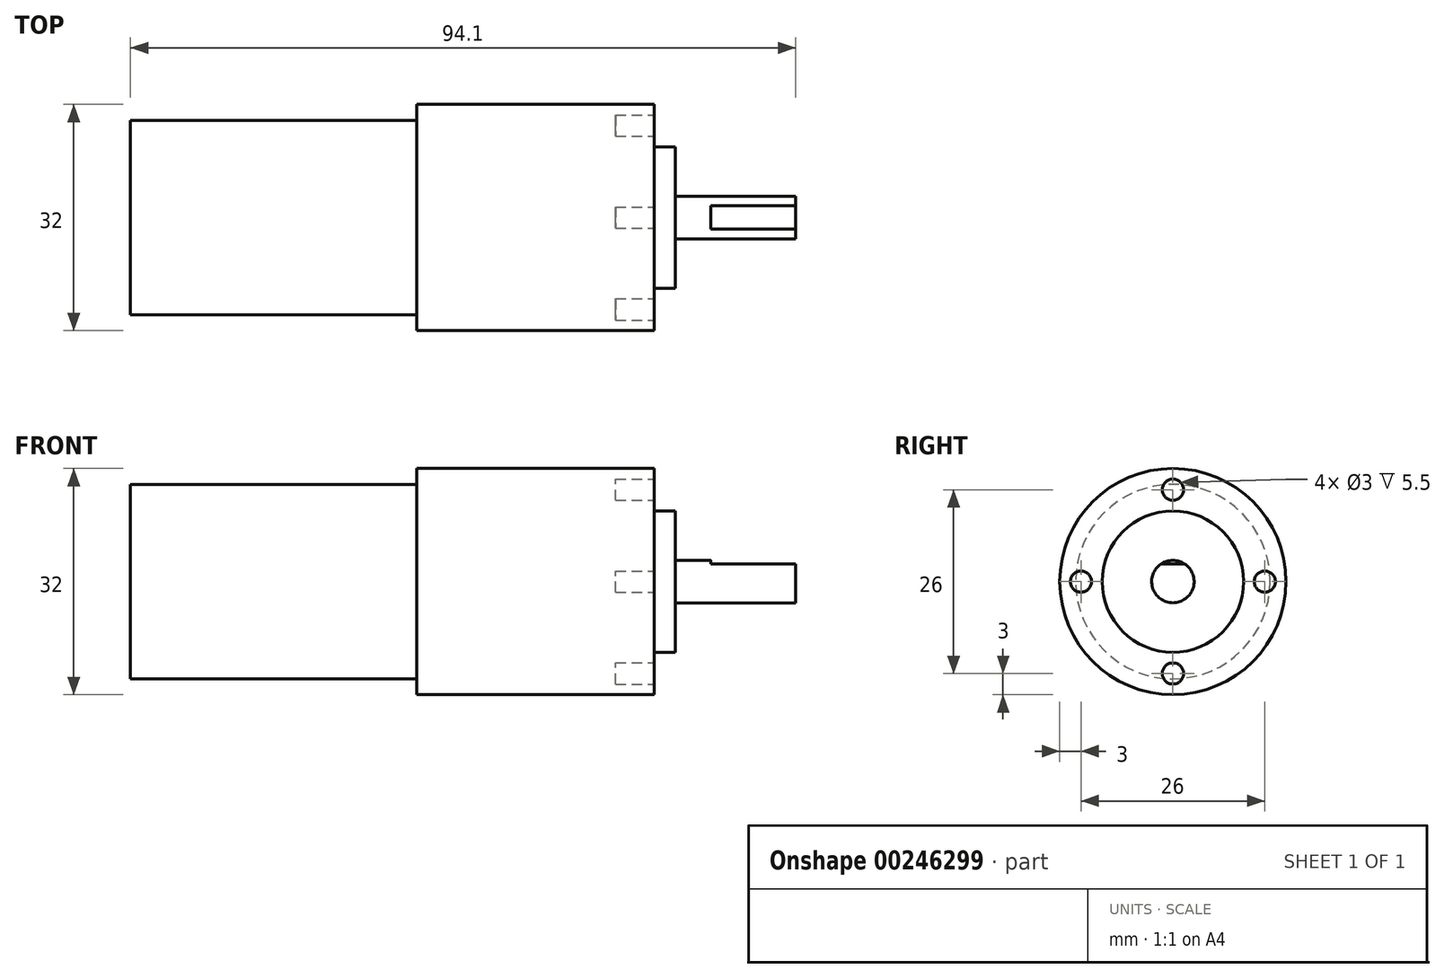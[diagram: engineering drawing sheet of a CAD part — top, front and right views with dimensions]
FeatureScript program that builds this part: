
annotation { "Feature Type Name" : "Feature", "Feature Type Description" : "" }
export const myFeature = defineFeature(function(context is Context, id is Id, definition is map)
    precondition{}
    {
        {
            var Q0;
            Q0=qCreatedBy(makeId("Right.planeOp"),FACE);
            var sketch = newSketch(context, id + "F0", { "sketchPlane" : qUnion([Q0])});
            skCircle(sketch, "E0", {"center": v(0, 0) * mm, "radius": 13.75 * mm});
            skSolve(sketch);
        }
        {
            var Q0;
            Q0 = qSketchRegion(id + "F0", true);
            extrude(context, id + "F1", {"entities" : qUnion([Q0]), "depth" : 40.5 * mm});
        }
        {
            var Q0;
            Q0=makeQuery(id+"F1.opExtrude","CAP_FACE",FACE,{"disambiguationData":[OSD([sQuery(id+"F0.wireOp",EDGE,"E0")])],"isStart":false});
            var sketch = newSketch(context, id + "F2", { "sketchPlane" : qUnion([Q0])});
            skCircle(sketch, "E1", {"center": v(0, 0) * mm, "radius": 16 * mm});
            skSolve(sketch);
        }
        {
            var Q0;
            Q0 = qSketchRegion(id + "F2", true);
            extrude(context, id + "F3", {"entities" : qUnion([Q0]), "operationType" : NewBodyOperationType.ADD, "depth" : 33.6 * mm});
        }
        {
            var Q0;
            Q0=makeQuery(id+"F3.opExtrude","CAP_FACE",FACE,{"disambiguationData":[OSD([sQuery(id+"F2.wireOp",EDGE,"E1")])],"isStart":false});
            var sketch = newSketch(context, id + "F4", { "sketchPlane" : qUnion([Q0])});
            skCircle(sketch, "E2", {"center": v(0, 0) * mm, "radius": 10 * mm});
            skSolve(sketch);
        }
        {
            var Q0;
            Q0 = qSketchRegion(id + "F4", true);
            extrude(context, id + "F5", {"entities" : qUnion([Q0]), "operationType" : NewBodyOperationType.ADD, "depth" : 3 * mm});
        }
        {
            var Q0;
            Q0=makeQuery(id+"F5.opExtrude","CAP_FACE",FACE,{"disambiguationData":[OSD([sQuery(id+"F4.wireOp",EDGE,"E2")])],"isStart":false});
            var sketch = newSketch(context, id + "F6", { "sketchPlane" : qUnion([Q0])});
            skCircle(sketch, "E3", {"center": v(0, 0) * mm, "radius": 3 * mm});
            skSolve(sketch);
        }
        {
            var Q0;
            Q0 = qSketchRegion(id + "F6", true);
            extrude(context, id + "F7", {"entities" : qUnion([Q0]), "operationType" : NewBodyOperationType.ADD, "depth" : 17 * mm});
        }
        {
            var Q0;
            Q0=makeQuery(id+"F7.opExtrude","CAP_FACE",FACE,{"disambiguationData":[OSD([sQuery(id+"F6.wireOp",EDGE,"E3")])],"isStart":false});
            var sketch = newSketch(context, id + "F8", { "sketchPlane" : qUnion([Q0])});
            skLineSegment(sketch, "E4.bottom", {"start": v(-4.78, 2.5) * mm, "end": v(4.95, 2.5) * mm});
            skLineSegment(sketch, "E4.top", {"start": v(-4.78, 5.79) * mm, "end": v(4.95, 5.79) * mm});
            skLineSegment(sketch, "E4.left", {"start": v(-4.78, 2.5) * mm, "end": v(-4.78, 5.79) * mm});
            skLineSegment(sketch, "E4.right", {"start": v(4.95, 2.5) * mm, "end": v(4.95, 5.79) * mm});
            skLineSegment(sketch, "E5", {"start": v(-6.95, -3) * mm, "end": v(35.62, -3) * mm});
            skSolve(sketch);
        }
        {
            var Q0;
            Q0 = qSketchRegion(id + "F8", true);
            extrude(context, id + "F9", {"entities" : qUnion([Q0]), "operationType" : NewBodyOperationType.REMOVE, "oppositeDirection" : true, "depth" : 12 * mm});
        }
        {
            var Q0;
            Q0=makeQuery(id+"F3.opExtrude","CAP_FACE",FACE,{"disambiguationData":[OSD([sQuery(id+"F2.wireOp",EDGE,"E1")])],"isStart":false});
            var sketch = newSketch(context, id + "F10", { "sketchPlane" : qUnion([Q0])});
            skCircle(sketch, "E6", {"center": v(0, 0) * mm, "radius": 13 * mm, "construction": true});
            skCircle(sketch, "E7", {"center": v(0, 13) * mm, "radius": 1.5 * mm});
            skCircle(sketch, "E8", {"center": v(13, 0) * mm, "radius": 1.5 * mm});
            skCircle(sketch, "E9", {"center": v(0, -13) * mm, "radius": 1.5 * mm});
            skCircle(sketch, "E10", {"center": v(-13, 0) * mm, "radius": 1.5 * mm});
            skSolve(sketch);
        }
        {
            var Q0;
            Q0 = qSketchRegion(id + "F10", true);
            extrude(context, id + "F11", {"entities" : qUnion([Q0]), "operationType" : NewBodyOperationType.REMOVE, "oppositeDirection" : true, "depth" : 5.5 * mm});
        }
    });
